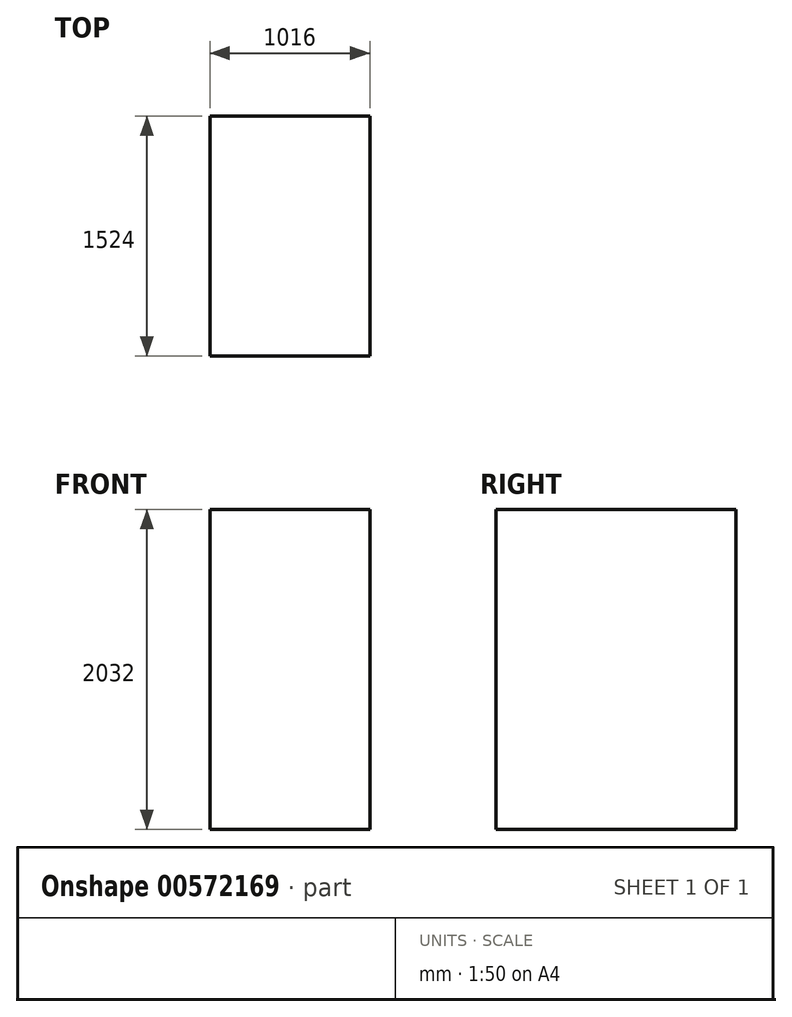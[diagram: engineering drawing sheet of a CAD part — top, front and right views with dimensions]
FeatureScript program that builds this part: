
annotation { "Feature Type Name" : "Feature", "Feature Type Description" : "" }
export const myFeature = defineFeature(function(context is Context, id is Id, definition is map)
    precondition{}
    {
        {
            var Q0;
            Q0=qCreatedBy(makeId("Top.planeOp"),FACE);
            var sketch = newSketch(context, id + "F0", { "sketchPlane" : qUnion([Q0])});
            skLineSegment(sketch, "E0.bottom", {"start": v(-982.61, 1502.94) * mm, "end": v(33.39, 1502.94) * mm});
            skLineSegment(sketch, "E0.top", {"start": v(-982.61, -21.06) * mm, "end": v(33.39, -21.06) * mm});
            skLineSegment(sketch, "E0.left", {"start": v(-982.61, 1502.94) * mm, "end": v(-982.61, -21.06) * mm});
            skLineSegment(sketch, "E0.right", {"start": v(33.39, 1502.94) * mm, "end": v(33.39, -21.06) * mm});
            skSolve(sketch);
        }
        {
            var Q0;
            Q0 = qSketchRegion(id + "F0", true);
            extrude(context, id + "F1", {"entities" : qUnion([Q0]), "depth" : 2032 * mm, "offsetDistance" : 25.4 * mm});
        }
    });
